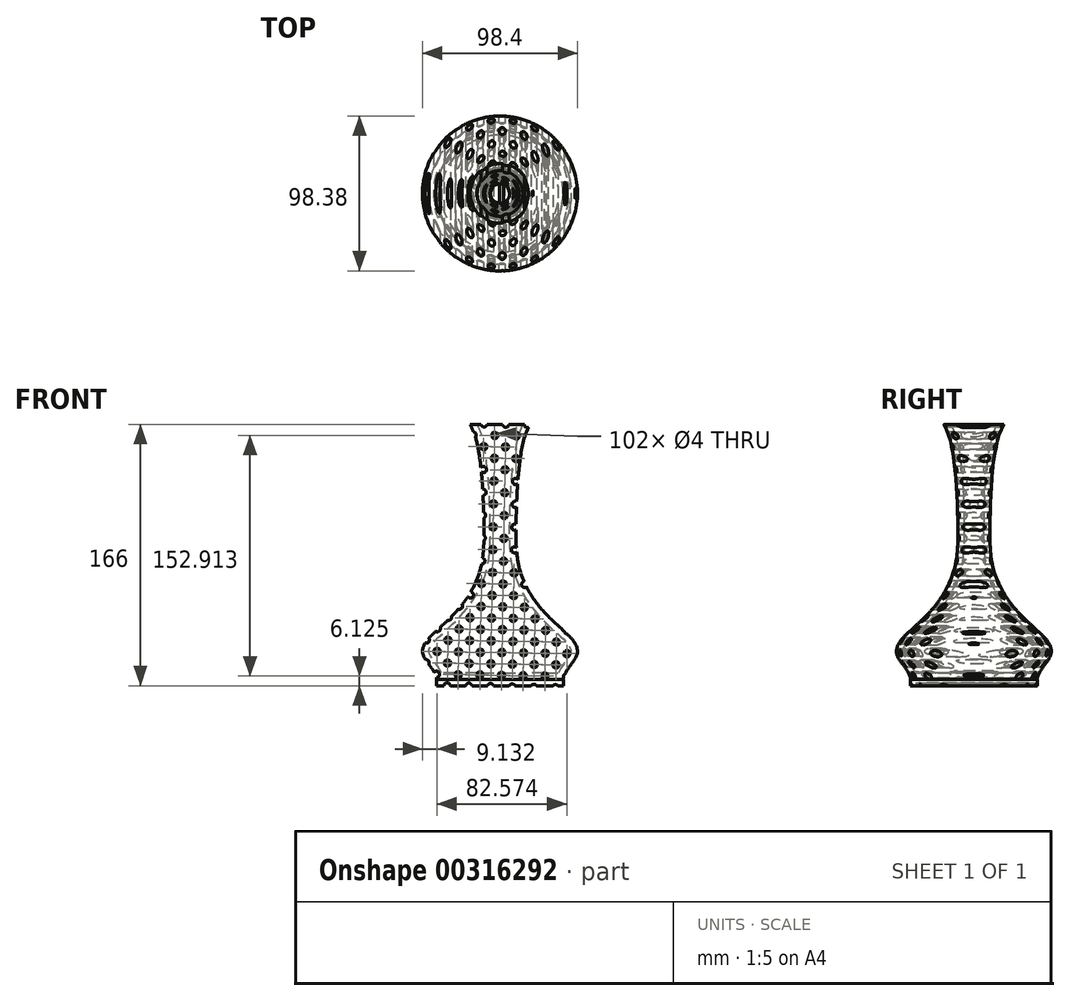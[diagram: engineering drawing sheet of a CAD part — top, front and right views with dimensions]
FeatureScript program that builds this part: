
annotation { "Feature Type Name" : "Feature", "Feature Type Description" : "" }
export const myFeature = defineFeature(function(context is Context, id is Id, definition is map)
    precondition{}
    {
        {
            var Q0;
            Q0=qCreatedBy(makeId("Top.planeOp"),FACE);
            var sketch = newSketch(context, id + "F0", { "sketchPlane" : qUnion([Q0])});
            skCircle(sketch, "E0", {"center": v(0, 0) * mm, "radius": 40 * mm});
            skSolve(sketch);
        }
        {
            var Q0;
            Q0=makeQuery(id+"F0.imprint","IMPRINT",FACE,{"disambiguationData":[TD([[makeQuery(id+"F0.imprint","IMPRINT",EDGE,{"derivedFrom":sQuery(id+"F0.wireOp",EDGE,"E0")}),1.0]])]});
            cPlane(context, id + "F1", {"entities" : qUnion([Q0]), "cplaneType" : CPlaneType.OFFSET, "offset" : 4 * mm, "width" : 150 * mm, "height" : 150 * mm});
        }
        {
            var Q0;
            Q0=qCreatedBy(id+"F1.planeOp",FACE);
            var sketch = newSketch(context, id + "F2", { "sketchPlane" : qUnion([Q0])});
            skCircle(sketch, "E1", {"center": v(0, 0) * mm, "radius": 41.51 * mm});
            skSolve(sketch);
        }
        {
            var Q0;
            Q0=makeQuery(id+"F2.imprint","IMPRINT",FACE,{"disambiguationData":[TD([[makeQuery(id+"F2.imprint","IMPRINT",EDGE,{"derivedFrom":sQuery(id+"F2.wireOp",EDGE,"E1")}),1.0]])]});
            cPlane(context, id + "F3", {"entities" : qUnion([Q0]), "cplaneType" : CPlaneType.OFFSET, "offset" : 6 * mm, "width" : 150 * mm, "height" : 150 * mm});
        }
        {
            var Q0;
            Q0=qCreatedBy(id+"F3.planeOp",FACE);
            var sketch = newSketch(context, id + "F4", { "sketchPlane" : qUnion([Q0])});
            skCircle(sketch, "E2", {"center": v(0, 0) * mm, "radius": 45.5 * mm});
            skSolve(sketch);
        }
        {
            var Q0;
            Q0=makeQuery(id+"F4.imprint","IMPRINT",FACE,{"disambiguationData":[TD([[makeQuery(id+"F4.imprint","IMPRINT",EDGE,{"derivedFrom":sQuery(id+"F4.wireOp",EDGE,"E2")}),1.0]])]});
            cPlane(context, id + "F5", {"entities" : qUnion([Q0]), "cplaneType" : CPlaneType.OFFSET, "offset" : 8 * mm, "width" : 150 * mm, "height" : 150 * mm});
        }
        {
            var Q0;
            Q0=qCreatedBy(id+"F5.planeOp",FACE);
            var sketch = newSketch(context, id + "F6", { "sketchPlane" : qUnion([Q0])});
            skCircle(sketch, "E3", {"center": v(0, 0) * mm, "radius": 49.2 * mm});
            skSolve(sketch);
        }
        {
            var Q0;
            Q0=makeQuery(id+"F6.imprint","IMPRINT",FACE,{"disambiguationData":[TD([[makeQuery(id+"F6.imprint","IMPRINT",EDGE,{"derivedFrom":sQuery(id+"F6.wireOp",EDGE,"E3")}),1.0]])]});
            cPlane(context, id + "F7", {"entities" : qUnion([Q0]), "cplaneType" : CPlaneType.OFFSET, "offset" : 6 * mm, "width" : 150 * mm, "height" : 150 * mm});
        }
        {
            var Q0;
            Q0=qCreatedBy(id+"F7.planeOp",FACE);
            var sketch = newSketch(context, id + "F8", { "sketchPlane" : qUnion([Q0])});
            skCircle(sketch, "E4", {"center": v(0, 0) * mm, "radius": 47 * mm});
            skSolve(sketch);
        }
        {
            var Q0;
            Q0=qCreatedBy(id+"F7.planeOp",FACE);
            cPlane(context, id + "F9", {"entities" : qUnion([Q0]), "cplaneType" : CPlaneType.OFFSET, "offset" : 6 * mm, "width" : 150 * mm, "height" : 150 * mm});
        }
        {
            var Q0;
            Q0=qCreatedBy(id+"F9.planeOp",FACE);
            var sketch = newSketch(context, id + "F10", { "sketchPlane" : qUnion([Q0])});
            skCircle(sketch, "E5", {"center": v(0, 0) * mm, "radius": 41.44 * mm});
            skSolve(sketch);
        }
        {
            var Q0;
            Q0=qCreatedBy(id+"F9.planeOp",FACE);
            cPlane(context, id + "F11", {"entities" : qUnion([Q0]), "cplaneType" : CPlaneType.OFFSET, "offset" : 16 * mm, "width" : 150 * mm, "height" : 150 * mm});
        }
        {
            var Q0;
            Q0=qCreatedBy(id+"F11.planeOp",FACE);
            var sketch = newSketch(context, id + "F12", { "sketchPlane" : qUnion([Q0])});
            skCircle(sketch, "E6", {"center": v(0, 0) * mm, "radius": 25.29 * mm});
            skSolve(sketch);
        }
        {
            var Q0;
            Q0=qCreatedBy(id+"F11.planeOp",FACE);
            cPlane(context, id + "F13", {"entities" : qUnion([Q0]), "cplaneType" : CPlaneType.OFFSET, "offset" : 25 * mm, "width" : 150 * mm, "height" : 150 * mm});
        }
        {
            var Q0;
            Q0=qCreatedBy(id+"F13.planeOp",FACE);
            var sketch = newSketch(context, id + "F14", { "sketchPlane" : qUnion([Q0])});
            skCircle(sketch, "E7", {"center": v(0, 0) * mm, "radius": 12.22 * mm});
            skSolve(sketch);
        }
        {
            var Q0;
            Q0=qCreatedBy(id+"F13.planeOp",FACE);
            cPlane(context, id + "F15", {"entities" : qUnion([Q0]), "cplaneType" : CPlaneType.OFFSET, "offset" : 25 * mm, "width" : 150 * mm, "height" : 150 * mm});
        }
        {
            var Q0;
            Q0=qCreatedBy(id+"F15.planeOp",FACE);
            var sketch = newSketch(context, id + "F16", { "sketchPlane" : qUnion([Q0])});
            skCircle(sketch, "E8", {"center": v(0, 0) * mm, "radius": 10.18 * mm});
            skSolve(sketch);
        }
        {
            var Q0;
            Q0=qCreatedBy(id+"F15.planeOp",FACE);
            cPlane(context, id + "F17", {"entities" : qUnion([Q0]), "cplaneType" : CPlaneType.OFFSET, "offset" : 25 * mm, "width" : 150 * mm, "height" : 150 * mm});
        }
        {
            var Q0;
            Q0=qCreatedBy(id+"F17.planeOp",FACE);
            var sketch = newSketch(context, id + "F18", { "sketchPlane" : qUnion([Q0])});
            skCircle(sketch, "E9", {"center": v(0, 0) * mm, "radius": 11 * mm});
            skSolve(sketch);
        }
        {
            var Q0;
            Q0=qCreatedBy(id+"F17.planeOp",FACE);
            cPlane(context, id + "F19", {"entities" : qUnion([Q0]), "cplaneType" : CPlaneType.OFFSET, "offset" : 25 * mm, "width" : 150 * mm, "height" : 150 * mm});
        }
        {
            var Q0;
            Q0=qCreatedBy(id+"F19.planeOp",FACE);
            var sketch = newSketch(context, id + "F20", { "sketchPlane" : qUnion([Q0])});
            skCircle(sketch, "E10", {"center": v(0, 0) * mm, "radius": 13.75 * mm});
            skSolve(sketch);
        }
        {
            var Q0;
            Q0=qCreatedBy(id+"F19.planeOp",FACE);
            cPlane(context, id + "F21", {"entities" : qUnion([Q0]), "cplaneType" : CPlaneType.OFFSET, "offset" : 10 * mm, "width" : 150 * mm, "height" : 150 * mm});
        }
        {
            var Q0;
            Q0=qCreatedBy(id+"F21.planeOp",FACE);
            var sketch = newSketch(context, id + "F22", { "sketchPlane" : qUnion([Q0])});
            skCircle(sketch, "E11", {"center": v(0, 0) * mm, "radius": 16.33 * mm});
            skSolve(sketch);
        }
        {
            var Q0;
            Q0=qCreatedBy(id+"F21.planeOp",FACE);
            cPlane(context, id + "F23", {"entities" : qUnion([Q0]), "cplaneType" : CPlaneType.OFFSET, "offset" : 6 * mm, "width" : 150 * mm, "height" : 150 * mm});
        }
        {
            var Q0;
            Q0=qCreatedBy(id+"F23.planeOp",FACE);
            var sketch = newSketch(context, id + "F24", { "sketchPlane" : qUnion([Q0])});
            skCircle(sketch, "E12", {"center": v(0, 0) * mm, "radius": 18.94 * mm});
            skSolve(sketch);
        }
        {
            var Q0;
            Q0=qSketchRegion(id+"F0",true);
            var Q1;
            Q1=qSketchRegion(id+"F2",true);
            var Q2;
            Q2=qSketchRegion(id+"F4",true);
            var Q3;
            Q3=qSketchRegion(id+"F6",true);
            var Q4;
            Q4=qSketchRegion(id+"F8",true);
            var Q5;
            Q5=qSketchRegion(id+"F10",true);
            var Q6;
            Q6=qSketchRegion(id+"F12",true);
            var Q7;
            Q7=qSketchRegion(id+"F14",true);
            var Q8;
            Q8=qSketchRegion(id+"F16",true);
            var Q9;
            Q9=qSketchRegion(id+"F18",true);
            var Q10;
            Q10=qSketchRegion(id+"F20",true);
            var Q11;
            Q11=qSketchRegion(id+"F22",true);
            var Q12;
            Q12=qSketchRegion(id+"F24",true);
            loft(context, id + "F25", {"sheetProfilesArray" : [{ "sheetProfileEntities" : qUnion([Q0]) }, { "sheetProfileEntities" : qUnion([Q1]) }, { "sheetProfileEntities" : qUnion([Q2]) }, { "sheetProfileEntities" : qUnion([Q3]) }, { "sheetProfileEntities" : qUnion([Q4]) }, { "sheetProfileEntities" : qUnion([Q5]) }, { "sheetProfileEntities" : qUnion([Q6]) }, { "sheetProfileEntities" : qUnion([Q7]) }, { "sheetProfileEntities" : qUnion([Q8]) }, { "sheetProfileEntities" : qUnion([Q9]) }, { "sheetProfileEntities" : qUnion([Q10]) }, { "sheetProfileEntities" : qUnion([Q11]) }, { "sheetProfileEntities" : qUnion([Q12]) }]});
        }
        {
            var Q0;
            Q0=makeQuery(id+"F25.opLoft","CAP_FACE",FACE,{"disambiguationData":[OSD([makeQuery(id+"F24.imprint","IMPRINT",FACE,{"disambiguationData":[TD([[makeQuery(id+"F24.imprint","IMPRINT",EDGE,{"derivedFrom":sQuery(id+"F24.wireOp",EDGE,"E12")}),1.0]])]})])],"isStart":true});
            shell(context, id + "F26", {"entities" : qUnion([Q0]), "thickness" : 4 * mm});
        }
        {
            var Q0;
            Q0=qCreatedBy(makeId("Top.planeOp"),FACE);
            var sketch = newSketch(context, id + "F27", { "sketchPlane" : qUnion([Q0])});
            skCircle(sketch, "E13", {"center": v(0, 0) * mm, "radius": 40.24 * mm});
            skSolve(sketch);
        }
        {
            var Q0;
            Q0=qSketchRegion(id+"F27",true);
            extrude(context, id + "F28", {"entities" : qUnion([Q0]), "operationType" : NewBodyOperationType.ADD, "oppositeDirection" : true, "depth" : 4 * mm});
        }
        {
            var Q0;
            Q0=qCreatedBy(makeId("Front.planeOp"),FACE);
            var sketch = newSketch(context, id + "F29", { "sketchPlane" : qUnion([Q0])});
            skCircle(sketch, "E14", {"center": v(0, -55.44) * mm, "radius": 2 * mm});
            skCircle(sketch, "E15.0.1.0", {"center": v(-6.76, -48.08) * mm, "radius": 2 * mm});
            skCircle(sketch, "E15.0.2.0", {"center": v(-13.52, -40.7) * mm, "radius": 2 * mm});
            skCircle(sketch, "E15.0.3.0", {"center": v(-20.28, -33.34) * mm, "radius": 2 * mm});
            skCircle(sketch, "E15.0.4.0", {"center": v(-27.04, -25.97) * mm, "radius": 2 * mm});
            skCircle(sketch, "E15.0.5.0", {"center": v(-33.8, -18.6) * mm, "radius": 2 * mm});
            skCircle(sketch, "E15.0.6.0", {"center": v(-40.56, -11.23) * mm, "radius": 2 * mm});
            skCircle(sketch, "E15.0.7.0", {"center": v(-47.32, -3.86) * mm, "radius": 2 * mm});
            skCircle(sketch, "E15.0.8.0", {"center": v(-54.07, 3.51) * mm, "radius": 2 * mm});
            skCircle(sketch, "E15.0.9.0", {"center": v(-60.83, 10.88) * mm, "radius": 2 * mm});
            skCircle(sketch, "E15.0.10.0", {"center": v(-67.6, 18.25) * mm, "radius": 2 * mm});
            skCircle(sketch, "E15.0.11.0", {"center": v(-74.35, 25.62) * mm, "radius": 2 * mm});
            skCircle(sketch, "E15.0.12.0", {"center": v(-81.11, 33) * mm, "radius": 2 * mm});
            skCircle(sketch, "E15.0.13.0", {"center": v(-87.87, 40.36) * mm, "radius": 2 * mm});
            skCircle(sketch, "E15.0.14.0", {"center": v(-94.63, 47.73) * mm, "radius": 2 * mm});
            skCircle(sketch, "E15.0.15.0", {"center": v(-101.39, 55.1) * mm, "radius": 2 * mm});
            skCircle(sketch, "E15.0.16.0", {"center": v(-108.15, 62.47) * mm, "radius": 2 * mm});
            skCircle(sketch, "E15.0.17.0", {"center": v(-114.9, 69.84) * mm, "radius": 2 * mm});
            skCircle(sketch, "E15.0.18.0", {"center": v(-121.67, 77.2) * mm, "radius": 2 * mm});
            skCircle(sketch, "E15.0.19.0", {"center": v(-128.43, 84.58) * mm, "radius": 2 * mm});
            skCircle(sketch, "E15.0.20.0", {"center": v(-135.19, 91.95) * mm, "radius": 2 * mm});
            skCircle(sketch, "E15.0.21.0", {"center": v(-141.95, 99.32) * mm, "radius": 2 * mm});
            skCircle(sketch, "E15.0.22.0", {"center": v(-148.7, 106.69) * mm, "radius": 2 * mm});
            skCircle(sketch, "E15.0.23.0", {"center": v(-155.46, 114.06) * mm, "radius": 2 * mm});
            skCircle(sketch, "E15.0.24.0", {"center": v(-162.22, 121.43) * mm, "radius": 2 * mm});
            skCircle(sketch, "E15.1.0.0", {"center": v(7, -48.3) * mm, "radius": 2 * mm});
            skCircle(sketch, "E15.1.1.0", {"center": v(0.24, -40.94) * mm, "radius": 2 * mm});
            skCircle(sketch, "E15.1.2.0", {"center": v(-6.52, -33.57) * mm, "radius": 2 * mm});
            skCircle(sketch, "E15.1.3.0", {"center": v(-13.27, -26.2) * mm, "radius": 2 * mm});
            skCircle(sketch, "E15.1.4.0", {"center": v(-20.03, -18.83) * mm, "radius": 2 * mm});
            skCircle(sketch, "E15.1.5.0", {"center": v(-26.8, -11.46) * mm, "radius": 2 * mm});
            skCircle(sketch, "E15.1.6.0", {"center": v(-33.55, -4.09) * mm, "radius": 2 * mm});
            skCircle(sketch, "E15.1.7.0", {"center": v(-40.31, 3.28) * mm, "radius": 2 * mm});
            skCircle(sketch, "E15.1.8.0", {"center": v(-47.07, 10.65) * mm, "radius": 2 * mm});
            skCircle(sketch, "E15.1.9.0", {"center": v(-53.83, 18.02) * mm, "radius": 2 * mm});
            skCircle(sketch, "E15.1.10.0", {"center": v(-60.6, 25.4) * mm, "radius": 2 * mm});
            skCircle(sketch, "E15.1.11.0", {"center": v(-67.35, 32.76) * mm, "radius": 2 * mm});
            skCircle(sketch, "E15.1.12.0", {"center": v(-74.1, 40.13) * mm, "radius": 2 * mm});
            skCircle(sketch, "E15.1.13.0", {"center": v(-80.87, 47.5) * mm, "radius": 2 * mm});
            skCircle(sketch, "E15.1.14.0", {"center": v(-87.63, 54.87) * mm, "radius": 2 * mm});
            skCircle(sketch, "E15.1.15.0", {"center": v(-94.39, 62.24) * mm, "radius": 2 * mm});
            skCircle(sketch, "E15.1.16.0", {"center": v(-101.15, 69.6) * mm, "radius": 2 * mm});
            skCircle(sketch, "E15.1.17.0", {"center": v(-107.9, 76.98) * mm, "radius": 2 * mm});
            skCircle(sketch, "E15.1.18.0", {"center": v(-114.66, 84.35) * mm, "radius": 2 * mm});
            skCircle(sketch, "E15.1.19.0", {"center": v(-121.42, 91.72) * mm, "radius": 2 * mm});
            skCircle(sketch, "E15.1.20.0", {"center": v(-128.18, 99.09) * mm, "radius": 2 * mm});
            skCircle(sketch, "E15.1.21.0", {"center": v(-134.94, 106.46) * mm, "radius": 2 * mm});
            skCircle(sketch, "E15.1.22.0", {"center": v(-141.7, 113.83) * mm, "radius": 2 * mm});
            skCircle(sketch, "E15.1.23.0", {"center": v(-148.46, 121.2) * mm, "radius": 2 * mm});
            skCircle(sketch, "E15.1.24.0", {"center": v(-155.22, 128.57) * mm, "radius": 2 * mm});
            skCircle(sketch, "E15.2.0.0", {"center": v(14, -41.17) * mm, "radius": 2 * mm});
            skCircle(sketch, "E15.2.1.0", {"center": v(7.25, -33.8) * mm, "radius": 2 * mm});
            skCircle(sketch, "E15.2.2.0", {"center": v(0.49, -26.43) * mm, "radius": 2 * mm});
            skCircle(sketch, "E15.2.3.0", {"center": v(-6.27, -19.06) * mm, "radius": 2 * mm});
            skCircle(sketch, "E15.2.4.0", {"center": v(-13.03, -11.69) * mm, "radius": 2 * mm});
            skCircle(sketch, "E15.2.5.0", {"center": v(-19.8, -4.32) * mm, "radius": 2 * mm});
            skCircle(sketch, "E15.2.6.0", {"center": v(-26.55, 3.05) * mm, "radius": 2 * mm});
            skCircle(sketch, "E15.2.7.0", {"center": v(-33.3, 10.42) * mm, "radius": 2 * mm});
            skCircle(sketch, "E15.2.8.0", {"center": v(-40.07, 17.79) * mm, "radius": 2 * mm});
            skCircle(sketch, "E15.2.9.0", {"center": v(-46.83, 25.16) * mm, "radius": 2 * mm});
            skCircle(sketch, "E15.2.10.0", {"center": v(-53.59, 32.53) * mm, "radius": 2 * mm});
            skCircle(sketch, "E15.2.11.0", {"center": v(-60.35, 39.9) * mm, "radius": 2 * mm});
            skCircle(sketch, "E15.2.12.0", {"center": v(-67.1, 47.27) * mm, "radius": 2 * mm});
            skCircle(sketch, "E15.2.13.0", {"center": v(-73.86, 54.64) * mm, "radius": 2 * mm});
            skCircle(sketch, "E15.2.14.0", {"center": v(-80.62, 62) * mm, "radius": 2 * mm});
            skCircle(sketch, "E15.2.15.0", {"center": v(-87.38, 69.38) * mm, "radius": 2 * mm});
            skCircle(sketch, "E15.2.16.0", {"center": v(-94.14, 76.75) * mm, "radius": 2 * mm});
            skCircle(sketch, "E15.2.17.0", {"center": v(-100.9, 84.12) * mm, "radius": 2 * mm});
            skCircle(sketch, "E15.2.18.0", {"center": v(-107.66, 91.49) * mm, "radius": 2 * mm});
            skCircle(sketch, "E15.2.19.0", {"center": v(-114.42, 98.86) * mm, "radius": 2 * mm});
            skCircle(sketch, "E15.2.20.0", {"center": v(-121.18, 106.23) * mm, "radius": 2 * mm});
            skCircle(sketch, "E15.2.21.0", {"center": v(-127.94, 113.6) * mm, "radius": 2 * mm});
            skCircle(sketch, "E15.2.22.0", {"center": v(-134.7, 120.96) * mm, "radius": 2 * mm});
            skCircle(sketch, "E15.2.23.0", {"center": v(-141.46, 128.33) * mm, "radius": 2 * mm});
            skCircle(sketch, "E15.2.24.0", {"center": v(-148.22, 135.7) * mm, "radius": 2 * mm});
            skCircle(sketch, "E15.3.0.0", {"center": v(21, -34.03) * mm, "radius": 2 * mm});
            skCircle(sketch, "E15.3.1.0", {"center": v(14.25, -26.66) * mm, "radius": 2 * mm});
            skCircle(sketch, "E15.3.2.0", {"center": v(7.5, -19.3) * mm, "radius": 2 * mm});
            skCircle(sketch, "E15.3.3.0", {"center": v(0.73, -11.92) * mm, "radius": 2 * mm});
            skCircle(sketch, "E15.3.4.0", {"center": v(-6.03, -4.55) * mm, "radius": 2 * mm});
            skCircle(sketch, "E15.3.5.0", {"center": v(-12.79, 2.82) * mm, "radius": 2 * mm});
            skCircle(sketch, "E15.3.6.0", {"center": v(-19.55, 10.19) * mm, "radius": 2 * mm});
            skCircle(sketch, "E15.3.7.0", {"center": v(-26.3, 17.56) * mm, "radius": 2 * mm});
            skCircle(sketch, "E15.3.8.0", {"center": v(-33.07, 24.93) * mm, "radius": 2 * mm});
            skCircle(sketch, "E15.3.9.0", {"center": v(-39.82, 32.3) * mm, "radius": 2 * mm});
            skCircle(sketch, "E15.3.10.0", {"center": v(-46.58, 39.67) * mm, "radius": 2 * mm});
            skCircle(sketch, "E15.3.11.0", {"center": v(-53.34, 47.04) * mm, "radius": 2 * mm});
            skCircle(sketch, "E15.3.12.0", {"center": v(-60.1, 54.4) * mm, "radius": 2 * mm});
            skCircle(sketch, "E15.3.13.0", {"center": v(-66.86, 61.78) * mm, "radius": 2 * mm});
            skCircle(sketch, "E15.3.14.0", {"center": v(-73.62, 69.15) * mm, "radius": 2 * mm});
            skCircle(sketch, "E15.3.15.0", {"center": v(-80.38, 76.52) * mm, "radius": 2 * mm});
            skCircle(sketch, "E15.3.16.0", {"center": v(-87.14, 83.89) * mm, "radius": 2 * mm});
            skCircle(sketch, "E15.3.17.0", {"center": v(-93.9, 91.25) * mm, "radius": 2 * mm});
            skCircle(sketch, "E15.3.18.0", {"center": v(-100.66, 98.62) * mm, "radius": 2 * mm});
            skCircle(sketch, "E15.3.19.0", {"center": v(-107.42, 106) * mm, "radius": 2 * mm});
            skCircle(sketch, "E15.3.20.0", {"center": v(-114.18, 113.36) * mm, "radius": 2 * mm});
            skCircle(sketch, "E15.3.21.0", {"center": v(-120.94, 120.73) * mm, "radius": 2 * mm});
            skCircle(sketch, "E15.3.22.0", {"center": v(-127.7, 128.1) * mm, "radius": 2 * mm});
            skCircle(sketch, "E15.3.23.0", {"center": v(-134.45, 135.47) * mm, "radius": 2 * mm});
            skCircle(sketch, "E15.3.24.0", {"center": v(-141.21, 142.84) * mm, "radius": 2 * mm});
            skCircle(sketch, "E15.4.0.0", {"center": v(28.01, -26.9) * mm, "radius": 2 * mm});
            skCircle(sketch, "E15.4.1.0", {"center": v(21.25, -19.52) * mm, "radius": 2 * mm});
            skCircle(sketch, "E15.4.2.0", {"center": v(14.5, -12.15) * mm, "radius": 2 * mm});
            skCircle(sketch, "E15.4.3.0", {"center": v(7.73, -4.78) * mm, "radius": 2 * mm});
            skCircle(sketch, "E15.4.4.0", {"center": v(0.97, 2.59) * mm, "radius": 2 * mm});
            skCircle(sketch, "E15.4.5.0", {"center": v(-5.78, 9.96) * mm, "radius": 2 * mm});
            skCircle(sketch, "E15.4.6.0", {"center": v(-12.54, 17.33) * mm, "radius": 2 * mm});
            skCircle(sketch, "E15.4.7.0", {"center": v(-19.3, 24.7) * mm, "radius": 2 * mm});
            skCircle(sketch, "E15.4.8.0", {"center": v(-26.06, 32.07) * mm, "radius": 2 * mm});
            skCircle(sketch, "E15.4.9.0", {"center": v(-32.82, 39.44) * mm, "radius": 2 * mm});
            skCircle(sketch, "E15.4.10.0", {"center": v(-39.58, 46.8) * mm, "radius": 2 * mm});
            skCircle(sketch, "E15.4.11.0", {"center": v(-46.34, 54.18) * mm, "radius": 2 * mm});
            skCircle(sketch, "E15.4.12.0", {"center": v(-53.1, 61.54) * mm, "radius": 2 * mm});
            skCircle(sketch, "E15.4.13.0", {"center": v(-59.86, 68.91) * mm, "radius": 2 * mm});
            skCircle(sketch, "E15.4.14.0", {"center": v(-66.62, 76.28) * mm, "radius": 2 * mm});
            skCircle(sketch, "E15.4.15.0", {"center": v(-73.38, 83.65) * mm, "radius": 2 * mm});
            skCircle(sketch, "E15.4.16.0", {"center": v(-80.14, 91.02) * mm, "radius": 2 * mm});
            skCircle(sketch, "E15.4.17.0", {"center": v(-86.9, 98.4) * mm, "radius": 2 * mm});
            skCircle(sketch, "E15.4.18.0", {"center": v(-93.66, 105.76) * mm, "radius": 2 * mm});
            skCircle(sketch, "E15.4.19.0", {"center": v(-100.41, 113.13) * mm, "radius": 2 * mm});
            skCircle(sketch, "E15.4.20.0", {"center": v(-107.17, 120.5) * mm, "radius": 2 * mm});
            skCircle(sketch, "E15.4.21.0", {"center": v(-113.93, 127.87) * mm, "radius": 2 * mm});
            skCircle(sketch, "E15.4.22.0", {"center": v(-120.7, 135.24) * mm, "radius": 2 * mm});
            skCircle(sketch, "E15.4.23.0", {"center": v(-127.45, 142.61) * mm, "radius": 2 * mm});
            skCircle(sketch, "E15.4.24.0", {"center": v(-134.21, 149.98) * mm, "radius": 2 * mm});
            skCircle(sketch, "E15.5.0.0", {"center": v(35.02, -19.75) * mm, "radius": 2 * mm});
            skCircle(sketch, "E15.5.1.0", {"center": v(28.26, -12.38) * mm, "radius": 2 * mm});
            skCircle(sketch, "E15.5.2.0", {"center": v(21.5, -5.01) * mm, "radius": 2 * mm});
            skCircle(sketch, "E15.5.3.0", {"center": v(14.74, 2.36) * mm, "radius": 2 * mm});
            skCircle(sketch, "E15.5.4.0", {"center": v(7.98, 9.73) * mm, "radius": 2 * mm});
            skCircle(sketch, "E15.5.5.0", {"center": v(1.22, 17.1) * mm, "radius": 2 * mm});
            skCircle(sketch, "E15.5.6.0", {"center": v(-5.54, 24.47) * mm, "radius": 2 * mm});
            skCircle(sketch, "E15.5.7.0", {"center": v(-12.3, 31.84) * mm, "radius": 2 * mm});
            skCircle(sketch, "E15.5.8.0", {"center": v(-19.06, 39.2) * mm, "radius": 2 * mm});
            skCircle(sketch, "E15.5.9.0", {"center": v(-25.82, 46.57) * mm, "radius": 2 * mm});
            skCircle(sketch, "E15.5.10.0", {"center": v(-32.58, 53.94) * mm, "radius": 2 * mm});
            skCircle(sketch, "E15.5.11.0", {"center": v(-39.34, 61.31) * mm, "radius": 2 * mm});
            skCircle(sketch, "E15.5.12.0", {"center": v(-46.1, 68.68) * mm, "radius": 2 * mm});
            skCircle(sketch, "E15.5.13.0", {"center": v(-52.86, 76.05) * mm, "radius": 2 * mm});
            skCircle(sketch, "E15.5.14.0", {"center": v(-59.62, 83.42) * mm, "radius": 2 * mm});
            skCircle(sketch, "E15.5.15.0", {"center": v(-66.37, 90.8) * mm, "radius": 2 * mm});
            skCircle(sketch, "E15.5.16.0", {"center": v(-73.13, 98.16) * mm, "radius": 2 * mm});
            skCircle(sketch, "E15.5.17.0", {"center": v(-79.9, 105.53) * mm, "radius": 2 * mm});
            skCircle(sketch, "E15.5.18.0", {"center": v(-86.65, 112.9) * mm, "radius": 2 * mm});
            skCircle(sketch, "E15.5.19.0", {"center": v(-93.41, 120.27) * mm, "radius": 2 * mm});
            skCircle(sketch, "E15.5.20.0", {"center": v(-100.17, 127.64) * mm, "radius": 2 * mm});
            skCircle(sketch, "E15.5.21.0", {"center": v(-106.93, 135.01) * mm, "radius": 2 * mm});
            skCircle(sketch, "E15.5.22.0", {"center": v(-113.69, 142.38) * mm, "radius": 2 * mm});
            skCircle(sketch, "E15.5.23.0", {"center": v(-120.45, 149.75) * mm, "radius": 2 * mm});
            skCircle(sketch, "E15.5.24.0", {"center": v(-127.2, 157.12) * mm, "radius": 2 * mm});
            skCircle(sketch, "E15.6.0.0", {"center": v(42.02, -12.61) * mm, "radius": 2 * mm});
            skCircle(sketch, "E15.6.1.0", {"center": v(35.26, -5.24) * mm, "radius": 2 * mm});
            skCircle(sketch, "E15.6.2.0", {"center": v(28.5, 2.13) * mm, "radius": 2 * mm});
            skCircle(sketch, "E15.6.3.0", {"center": v(21.74, 9.5) * mm, "radius": 2 * mm});
            skCircle(sketch, "E15.6.4.0", {"center": v(14.98, 16.86) * mm, "radius": 2 * mm});
            skCircle(sketch, "E15.6.5.0", {"center": v(8.22, 24.23) * mm, "radius": 2 * mm});
            skCircle(sketch, "E15.6.6.0", {"center": v(1.46, 31.6) * mm, "radius": 2 * mm});
            skCircle(sketch, "E15.6.7.0", {"center": v(-5.3, 38.97) * mm, "radius": 2 * mm});
            skCircle(sketch, "E15.6.8.0", {"center": v(-12.06, 46.34) * mm, "radius": 2 * mm});
            skCircle(sketch, "E15.6.9.0", {"center": v(-18.82, 53.71) * mm, "radius": 2 * mm});
            skCircle(sketch, "E15.6.10.0", {"center": v(-25.57, 61.08) * mm, "radius": 2 * mm});
            skCircle(sketch, "E15.6.11.0", {"center": v(-32.33, 68.45) * mm, "radius": 2 * mm});
            skCircle(sketch, "E15.6.12.0", {"center": v(-39.1, 75.82) * mm, "radius": 2 * mm});
            skCircle(sketch, "E15.6.13.0", {"center": v(-45.85, 83.2) * mm, "radius": 2 * mm});
            skCircle(sketch, "E15.6.14.0", {"center": v(-52.61, 90.56) * mm, "radius": 2 * mm});
            skCircle(sketch, "E15.6.15.0", {"center": v(-59.37, 97.93) * mm, "radius": 2 * mm});
            skCircle(sketch, "E15.6.16.0", {"center": v(-66.13, 105.3) * mm, "radius": 2 * mm});
            skCircle(sketch, "E15.6.17.0", {"center": v(-72.9, 112.67) * mm, "radius": 2 * mm});
            skCircle(sketch, "E15.6.18.0", {"center": v(-79.65, 120.04) * mm, "radius": 2 * mm});
            skCircle(sketch, "E15.6.19.0", {"center": v(-86.4, 127.4) * mm, "radius": 2 * mm});
            skCircle(sketch, "E15.6.20.0", {"center": v(-93.17, 134.78) * mm, "radius": 2 * mm});
            skCircle(sketch, "E15.6.21.0", {"center": v(-99.93, 142.15) * mm, "radius": 2 * mm});
            skCircle(sketch, "E15.6.22.0", {"center": v(-106.69, 149.52) * mm, "radius": 2 * mm});
            skCircle(sketch, "E15.6.23.0", {"center": v(-113.45, 156.89) * mm, "radius": 2 * mm});
            skCircle(sketch, "E15.6.24.0", {"center": v(-120.2, 164.26) * mm, "radius": 2 * mm});
            skCircle(sketch, "E15.7.0.0", {"center": v(49.02, -5.48) * mm, "radius": 2 * mm});
            skCircle(sketch, "E15.7.1.0", {"center": v(42.26, 1.9) * mm, "radius": 2 * mm});
            skCircle(sketch, "E15.7.2.0", {"center": v(35.5, 9.26) * mm, "radius": 2 * mm});
            skCircle(sketch, "E15.7.3.0", {"center": v(28.74, 16.63) * mm, "radius": 2 * mm});
            skCircle(sketch, "E15.7.4.0", {"center": v(21.98, 24) * mm, "radius": 2 * mm});
            skCircle(sketch, "E15.7.5.0", {"center": v(15.22, 31.37) * mm, "radius": 2 * mm});
            skCircle(sketch, "E15.7.6.0", {"center": v(8.47, 38.74) * mm, "radius": 2 * mm});
            skCircle(sketch, "E15.7.7.0", {"center": v(1.7, 46.11) * mm, "radius": 2 * mm});
            skCircle(sketch, "E15.7.8.0", {"center": v(-5.05, 53.48) * mm, "radius": 2 * mm});
            skCircle(sketch, "E15.7.9.0", {"center": v(-11.81, 60.85) * mm, "radius": 2 * mm});
            skCircle(sketch, "E15.7.10.0", {"center": v(-18.57, 68.22) * mm, "radius": 2 * mm});
            skCircle(sketch, "E15.7.11.0", {"center": v(-25.33, 75.6) * mm, "radius": 2 * mm});
            skCircle(sketch, "E15.7.12.0", {"center": v(-32.1, 82.96) * mm, "radius": 2 * mm});
            skCircle(sketch, "E15.7.13.0", {"center": v(-38.85, 90.33) * mm, "radius": 2 * mm});
            skCircle(sketch, "E15.7.14.0", {"center": v(-45.6, 97.7) * mm, "radius": 2 * mm});
            skCircle(sketch, "E15.7.15.0", {"center": v(-52.37, 105.07) * mm, "radius": 2 * mm});
            skCircle(sketch, "E15.7.16.0", {"center": v(-59.13, 112.44) * mm, "radius": 2 * mm});
            skCircle(sketch, "E15.7.17.0", {"center": v(-65.89, 119.8) * mm, "radius": 2 * mm});
            skCircle(sketch, "E15.7.18.0", {"center": v(-72.65, 127.18) * mm, "radius": 2 * mm});
            skCircle(sketch, "E15.7.19.0", {"center": v(-79.4, 134.55) * mm, "radius": 2 * mm});
            skCircle(sketch, "E15.7.20.0", {"center": v(-86.16, 141.92) * mm, "radius": 2 * mm});
            skCircle(sketch, "E15.7.21.0", {"center": v(-92.92, 149.29) * mm, "radius": 2 * mm});
            skCircle(sketch, "E15.7.22.0", {"center": v(-99.68, 156.66) * mm, "radius": 2 * mm});
            skCircle(sketch, "E15.7.23.0", {"center": v(-106.44, 164.03) * mm, "radius": 2 * mm});
            skCircle(sketch, "E15.7.24.0", {"center": v(-113.2, 171.4) * mm, "radius": 2 * mm});
            skCircle(sketch, "E15.8.0.0", {"center": v(56.02, 1.66) * mm, "radius": 2 * mm});
            skCircle(sketch, "E15.8.1.0", {"center": v(49.26, 9.03) * mm, "radius": 2 * mm});
            skCircle(sketch, "E15.8.2.0", {"center": v(42.5, 16.4) * mm, "radius": 2 * mm});
            skCircle(sketch, "E15.8.3.0", {"center": v(35.75, 23.77) * mm, "radius": 2 * mm});
            skCircle(sketch, "E15.8.4.0", {"center": v(28.99, 31.14) * mm, "radius": 2 * mm});
            skCircle(sketch, "E15.8.5.0", {"center": v(22.23, 38.51) * mm, "radius": 2 * mm});
            skCircle(sketch, "E15.8.6.0", {"center": v(15.47, 45.88) * mm, "radius": 2 * mm});
            skCircle(sketch, "E15.8.7.0", {"center": v(8.7, 53.25) * mm, "radius": 2 * mm});
            skCircle(sketch, "E15.8.8.0", {"center": v(1.95, 60.62) * mm, "radius": 2 * mm});
            skCircle(sketch, "E15.8.9.0", {"center": v(-4.8, 67.99) * mm, "radius": 2 * mm});
            skCircle(sketch, "E15.8.10.0", {"center": v(-11.57, 75.36) * mm, "radius": 2 * mm});
            skCircle(sketch, "E15.8.11.0", {"center": v(-18.33, 82.73) * mm, "radius": 2 * mm});
            skCircle(sketch, "E15.8.12.0", {"center": v(-25.09, 90.1) * mm, "radius": 2 * mm});
            skCircle(sketch, "E15.8.13.0", {"center": v(-31.85, 97.47) * mm, "radius": 2 * mm});
            skCircle(sketch, "E15.8.14.0", {"center": v(-38.6, 104.84) * mm, "radius": 2 * mm});
            skCircle(sketch, "E15.8.15.0", {"center": v(-45.37, 112.2) * mm, "radius": 2 * mm});
            skCircle(sketch, "E15.8.16.0", {"center": v(-52.12, 119.58) * mm, "radius": 2 * mm});
            skCircle(sketch, "E15.8.17.0", {"center": v(-58.88, 126.95) * mm, "radius": 2 * mm});
            skCircle(sketch, "E15.8.18.0", {"center": v(-65.64, 134.32) * mm, "radius": 2 * mm});
            skCircle(sketch, "E15.8.19.0", {"center": v(-72.4, 141.69) * mm, "radius": 2 * mm});
            skCircle(sketch, "E15.8.20.0", {"center": v(-79.16, 149.06) * mm, "radius": 2 * mm});
            skCircle(sketch, "E15.8.21.0", {"center": v(-85.92, 156.43) * mm, "radius": 2 * mm});
            skCircle(sketch, "E15.8.22.0", {"center": v(-92.68, 163.8) * mm, "radius": 2 * mm});
            skCircle(sketch, "E15.8.23.0", {"center": v(-99.44, 171.16) * mm, "radius": 2 * mm});
            skCircle(sketch, "E15.8.24.0", {"center": v(-106.2, 178.53) * mm, "radius": 2 * mm});
            skCircle(sketch, "E15.9.0.0", {"center": v(63.03, 8.8) * mm, "radius": 2 * mm});
            skCircle(sketch, "E15.9.1.0", {"center": v(56.27, 16.17) * mm, "radius": 2 * mm});
            skCircle(sketch, "E15.9.2.0", {"center": v(49.5, 23.54) * mm, "radius": 2 * mm});
            skCircle(sketch, "E15.9.3.0", {"center": v(42.75, 30.91) * mm, "radius": 2 * mm});
            skCircle(sketch, "E15.9.4.0", {"center": v(36, 38.28) * mm, "radius": 2 * mm});
            skCircle(sketch, "E15.9.5.0", {"center": v(29.23, 45.65) * mm, "radius": 2 * mm});
            skCircle(sketch, "E15.9.6.0", {"center": v(22.47, 53.02) * mm, "radius": 2 * mm});
            skCircle(sketch, "E15.9.7.0", {"center": v(15.71, 60.39) * mm, "radius": 2 * mm});
            skCircle(sketch, "E15.9.8.0", {"center": v(8.95, 67.76) * mm, "radius": 2 * mm});
            skCircle(sketch, "E15.9.9.0", {"center": v(2.2, 75.13) * mm, "radius": 2 * mm});
            skCircle(sketch, "E15.9.10.0", {"center": v(-4.57, 82.5) * mm, "radius": 2 * mm});
            skCircle(sketch, "E15.9.11.0", {"center": v(-11.33, 89.87) * mm, "radius": 2 * mm});
            skCircle(sketch, "E15.9.12.0", {"center": v(-18.08, 97.24) * mm, "radius": 2 * mm});
            skCircle(sketch, "E15.9.13.0", {"center": v(-24.84, 104.6) * mm, "radius": 2 * mm});
            skCircle(sketch, "E15.9.14.0", {"center": v(-31.6, 111.98) * mm, "radius": 2 * mm});
            skCircle(sketch, "E15.9.15.0", {"center": v(-38.36, 119.35) * mm, "radius": 2 * mm});
            skCircle(sketch, "E15.9.16.0", {"center": v(-45.12, 126.72) * mm, "radius": 2 * mm});
            skCircle(sketch, "E15.9.17.0", {"center": v(-51.88, 134.09) * mm, "radius": 2 * mm});
            skCircle(sketch, "E15.9.18.0", {"center": v(-58.64, 141.46) * mm, "radius": 2 * mm});
            skCircle(sketch, "E15.9.19.0", {"center": v(-65.4, 148.82) * mm, "radius": 2 * mm});
            skCircle(sketch, "E15.9.20.0", {"center": v(-72.16, 156.2) * mm, "radius": 2 * mm});
            skCircle(sketch, "E15.9.21.0", {"center": v(-78.92, 163.56) * mm, "radius": 2 * mm});
            skCircle(sketch, "E15.9.22.0", {"center": v(-85.68, 170.93) * mm, "radius": 2 * mm});
            skCircle(sketch, "E15.9.23.0", {"center": v(-92.44, 178.3) * mm, "radius": 2 * mm});
            skCircle(sketch, "E15.9.24.0", {"center": v(-99.2, 185.67) * mm, "radius": 2 * mm});
            skCircle(sketch, "E15.10.0.0", {"center": v(70.03, 15.94) * mm, "radius": 2 * mm});
            skCircle(sketch, "E15.10.1.0", {"center": v(63.27, 23.3) * mm, "radius": 2 * mm});
            skCircle(sketch, "E15.10.2.0", {"center": v(56.51, 30.68) * mm, "radius": 2 * mm});
            skCircle(sketch, "E15.10.3.0", {"center": v(49.75, 38.05) * mm, "radius": 2 * mm});
            skCircle(sketch, "E15.10.4.0", {"center": v(43, 45.42) * mm, "radius": 2 * mm});
            skCircle(sketch, "E15.10.5.0", {"center": v(36.23, 52.79) * mm, "radius": 2 * mm});
            skCircle(sketch, "E15.10.6.0", {"center": v(29.47, 60.16) * mm, "radius": 2 * mm});
            skCircle(sketch, "E15.10.7.0", {"center": v(22.72, 67.53) * mm, "radius": 2 * mm});
            skCircle(sketch, "E15.10.8.0", {"center": v(15.96, 74.9) * mm, "radius": 2 * mm});
            skCircle(sketch, "E15.10.9.0", {"center": v(9.2, 82.27) * mm, "radius": 2 * mm});
            skCircle(sketch, "E15.10.10.0", {"center": v(2.44, 89.64) * mm, "radius": 2 * mm});
            skCircle(sketch, "E15.10.11.0", {"center": v(-4.32, 97) * mm, "radius": 2 * mm});
            skCircle(sketch, "E15.10.12.0", {"center": v(-11.08, 104.38) * mm, "radius": 2 * mm});
            skCircle(sketch, "E15.10.13.0", {"center": v(-17.84, 111.75) * mm, "radius": 2 * mm});
            skCircle(sketch, "E15.10.14.0", {"center": v(-24.6, 119.11) * mm, "radius": 2 * mm});
            skCircle(sketch, "E15.10.15.0", {"center": v(-31.36, 126.48) * mm, "radius": 2 * mm});
            skCircle(sketch, "E15.10.16.0", {"center": v(-38.12, 133.85) * mm, "radius": 2 * mm});
            skCircle(sketch, "E15.10.17.0", {"center": v(-44.88, 141.22) * mm, "radius": 2 * mm});
            skCircle(sketch, "E15.10.18.0", {"center": v(-51.64, 148.6) * mm, "radius": 2 * mm});
            skCircle(sketch, "E15.10.19.0", {"center": v(-58.4, 155.96) * mm, "radius": 2 * mm});
            skCircle(sketch, "E15.10.20.0", {"center": v(-65.16, 163.33) * mm, "radius": 2 * mm});
            skCircle(sketch, "E15.10.21.0", {"center": v(-71.92, 170.7) * mm, "radius": 2 * mm});
            skCircle(sketch, "E15.10.22.0", {"center": v(-78.67, 178.07) * mm, "radius": 2 * mm});
            skCircle(sketch, "E15.10.23.0", {"center": v(-85.43, 185.44) * mm, "radius": 2 * mm});
            skCircle(sketch, "E15.10.24.0", {"center": v(-92.2, 192.81) * mm, "radius": 2 * mm});
            skCircle(sketch, "E15.11.0.0", {"center": v(77.03, 23.08) * mm, "radius": 2 * mm});
            skCircle(sketch, "E15.11.1.0", {"center": v(70.27, 30.45) * mm, "radius": 2 * mm});
            skCircle(sketch, "E15.11.2.0", {"center": v(63.51, 37.82) * mm, "radius": 2 * mm});
            skCircle(sketch, "E15.11.3.0", {"center": v(56.76, 45.19) * mm, "radius": 2 * mm});
            skCircle(sketch, "E15.11.4.0", {"center": v(50, 52.56) * mm, "radius": 2 * mm});
            skCircle(sketch, "E15.11.5.0", {"center": v(43.24, 59.93) * mm, "radius": 2 * mm});
            skCircle(sketch, "E15.11.6.0", {"center": v(36.48, 67.3) * mm, "radius": 2 * mm});
            skCircle(sketch, "E15.11.7.0", {"center": v(29.72, 74.67) * mm, "radius": 2 * mm});
            skCircle(sketch, "E15.11.8.0", {"center": v(22.96, 82.04) * mm, "radius": 2 * mm});
            skCircle(sketch, "E15.11.9.0", {"center": v(16.2, 89.4) * mm, "radius": 2 * mm});
            skCircle(sketch, "E15.11.10.0", {"center": v(9.44, 96.77) * mm, "radius": 2 * mm});
            skCircle(sketch, "E15.11.11.0", {"center": v(2.68, 104.14) * mm, "radius": 2 * mm});
            skCircle(sketch, "E15.11.12.0", {"center": v(-4.08, 111.51) * mm, "radius": 2 * mm});
            skCircle(sketch, "E15.11.13.0", {"center": v(-10.84, 118.88) * mm, "radius": 2 * mm});
            skCircle(sketch, "E15.11.14.0", {"center": v(-17.6, 126.25) * mm, "radius": 2 * mm});
            skCircle(sketch, "E15.11.15.0", {"center": v(-24.36, 133.62) * mm, "radius": 2 * mm});
            skCircle(sketch, "E15.11.16.0", {"center": v(-31.12, 141) * mm, "radius": 2 * mm});
            skCircle(sketch, "E15.11.17.0", {"center": v(-37.87, 148.36) * mm, "radius": 2 * mm});
            skCircle(sketch, "E15.11.18.0", {"center": v(-44.63, 155.73) * mm, "radius": 2 * mm});
            skCircle(sketch, "E15.11.19.0", {"center": v(-51.4, 163.1) * mm, "radius": 2 * mm});
            skCircle(sketch, "E15.11.20.0", {"center": v(-58.15, 170.47) * mm, "radius": 2 * mm});
            skCircle(sketch, "E15.11.21.0", {"center": v(-64.91, 177.84) * mm, "radius": 2 * mm});
            skCircle(sketch, "E15.11.22.0", {"center": v(-71.67, 185.21) * mm, "radius": 2 * mm});
            skCircle(sketch, "E15.11.23.0", {"center": v(-78.43, 192.58) * mm, "radius": 2 * mm});
            skCircle(sketch, "E15.11.24.0", {"center": v(-85.2, 199.95) * mm, "radius": 2 * mm});
            skCircle(sketch, "E15.12.0.0", {"center": v(84.04, 30.22) * mm, "radius": 2 * mm});
            skCircle(sketch, "E15.12.1.0", {"center": v(77.28, 37.59) * mm, "radius": 2 * mm});
            skCircle(sketch, "E15.12.2.0", {"center": v(70.52, 44.96) * mm, "radius": 2 * mm});
            skCircle(sketch, "E15.12.3.0", {"center": v(63.76, 52.33) * mm, "radius": 2 * mm});
            skCircle(sketch, "E15.12.4.0", {"center": v(57, 59.7) * mm, "radius": 2 * mm});
            skCircle(sketch, "E15.12.5.0", {"center": v(50.24, 67.06) * mm, "radius": 2 * mm});
            skCircle(sketch, "E15.12.6.0", {"center": v(43.48, 74.43) * mm, "radius": 2 * mm});
            skCircle(sketch, "E15.12.7.0", {"center": v(36.72, 81.8) * mm, "radius": 2 * mm});
            skCircle(sketch, "E15.12.8.0", {"center": v(29.96, 89.17) * mm, "radius": 2 * mm});
            skCircle(sketch, "E15.12.9.0", {"center": v(23.2, 96.54) * mm, "radius": 2 * mm});
            skCircle(sketch, "E15.12.10.0", {"center": v(16.44, 103.91) * mm, "radius": 2 * mm});
            skCircle(sketch, "E15.12.11.0", {"center": v(9.68, 111.28) * mm, "radius": 2 * mm});
            skCircle(sketch, "E15.12.12.0", {"center": v(2.92, 118.65) * mm, "radius": 2 * mm});
            skCircle(sketch, "E15.12.13.0", {"center": v(-3.83, 126.02) * mm, "radius": 2 * mm});
            skCircle(sketch, "E15.12.14.0", {"center": v(-10.6, 133.4) * mm, "radius": 2 * mm});
            skCircle(sketch, "E15.12.15.0", {"center": v(-17.35, 140.76) * mm, "radius": 2 * mm});
            skCircle(sketch, "E15.12.16.0", {"center": v(-24.11, 148.13) * mm, "radius": 2 * mm});
            skCircle(sketch, "E15.12.17.0", {"center": v(-30.87, 155.5) * mm, "radius": 2 * mm});
            skCircle(sketch, "E15.12.18.0", {"center": v(-37.63, 162.87) * mm, "radius": 2 * mm});
            skCircle(sketch, "E15.12.19.0", {"center": v(-44.4, 170.24) * mm, "radius": 2 * mm});
            skCircle(sketch, "E15.12.20.0", {"center": v(-51.15, 177.6) * mm, "radius": 2 * mm});
            skCircle(sketch, "E15.12.21.0", {"center": v(-57.9, 184.98) * mm, "radius": 2 * mm});
            skCircle(sketch, "E15.12.22.0", {"center": v(-64.67, 192.35) * mm, "radius": 2 * mm});
            skCircle(sketch, "E15.12.23.0", {"center": v(-71.43, 199.72) * mm, "radius": 2 * mm});
            skCircle(sketch, "E15.12.24.0", {"center": v(-78.19, 207.09) * mm, "radius": 2 * mm});
            skCircle(sketch, "E15.13.0.0", {"center": v(91.04, 37.36) * mm, "radius": 2 * mm});
            skCircle(sketch, "E15.13.1.0", {"center": v(84.28, 44.72) * mm, "radius": 2 * mm});
            skCircle(sketch, "E15.13.2.0", {"center": v(77.52, 52.1) * mm, "radius": 2 * mm});
            skCircle(sketch, "E15.13.3.0", {"center": v(70.76, 59.46) * mm, "radius": 2 * mm});
            skCircle(sketch, "E15.13.4.0", {"center": v(64, 66.83) * mm, "radius": 2 * mm});
            skCircle(sketch, "E15.13.5.0", {"center": v(57.24, 74.2) * mm, "radius": 2 * mm});
            skCircle(sketch, "E15.13.6.0", {"center": v(50.48, 81.57) * mm, "radius": 2 * mm});
            skCircle(sketch, "E15.13.7.0", {"center": v(43.72, 88.94) * mm, "radius": 2 * mm});
            skCircle(sketch, "E15.13.8.0", {"center": v(36.96, 96.31) * mm, "radius": 2 * mm});
            skCircle(sketch, "E15.13.9.0", {"center": v(30.2, 103.68) * mm, "radius": 2 * mm});
            skCircle(sketch, "E15.13.10.0", {"center": v(23.45, 111.05) * mm, "radius": 2 * mm});
            skCircle(sketch, "E15.13.11.0", {"center": v(16.69, 118.42) * mm, "radius": 2 * mm});
            skCircle(sketch, "E15.13.12.0", {"center": v(9.93, 125.8) * mm, "radius": 2 * mm});
            skCircle(sketch, "E15.13.13.0", {"center": v(3.17, 133.16) * mm, "radius": 2 * mm});
            skCircle(sketch, "E15.13.14.0", {"center": v(-3.6, 140.53) * mm, "radius": 2 * mm});
            skCircle(sketch, "E15.13.15.0", {"center": v(-10.35, 147.9) * mm, "radius": 2 * mm});
            skCircle(sketch, "E15.13.16.0", {"center": v(-17.1, 155.27) * mm, "radius": 2 * mm});
            skCircle(sketch, "E15.13.17.0", {"center": v(-23.87, 162.64) * mm, "radius": 2 * mm});
            skCircle(sketch, "E15.13.18.0", {"center": v(-30.63, 170) * mm, "radius": 2 * mm});
            skCircle(sketch, "E15.13.19.0", {"center": v(-37.39, 177.38) * mm, "radius": 2 * mm});
            skCircle(sketch, "E15.13.20.0", {"center": v(-44.15, 184.75) * mm, "radius": 2 * mm});
            skCircle(sketch, "E15.13.21.0", {"center": v(-50.9, 192.12) * mm, "radius": 2 * mm});
            skCircle(sketch, "E15.13.22.0", {"center": v(-57.67, 199.49) * mm, "radius": 2 * mm});
            skCircle(sketch, "E15.13.23.0", {"center": v(-64.42, 206.86) * mm, "radius": 2 * mm});
            skCircle(sketch, "E15.13.24.0", {"center": v(-71.18, 214.23) * mm, "radius": 2 * mm});
            skCircle(sketch, "E15.14.0.0", {"center": v(98.04, 44.5) * mm, "radius": 2 * mm});
            skCircle(sketch, "E15.14.1.0", {"center": v(91.28, 51.86) * mm, "radius": 2 * mm});
            skCircle(sketch, "E15.14.2.0", {"center": v(84.52, 59.23) * mm, "radius": 2 * mm});
            skCircle(sketch, "E15.14.3.0", {"center": v(77.76, 66.6) * mm, "radius": 2 * mm});
            skCircle(sketch, "E15.14.4.0", {"center": v(71, 73.97) * mm, "radius": 2 * mm});
            skCircle(sketch, "E15.14.5.0", {"center": v(64.25, 81.34) * mm, "radius": 2 * mm});
            skCircle(sketch, "E15.14.6.0", {"center": v(57.49, 88.71) * mm, "radius": 2 * mm});
            skCircle(sketch, "E15.14.7.0", {"center": v(50.73, 96.08) * mm, "radius": 2 * mm});
            skCircle(sketch, "E15.14.8.0", {"center": v(43.97, 103.45) * mm, "radius": 2 * mm});
            skCircle(sketch, "E15.14.9.0", {"center": v(37.2, 110.82) * mm, "radius": 2 * mm});
            skCircle(sketch, "E15.14.10.0", {"center": v(30.45, 118.2) * mm, "radius": 2 * mm});
            skCircle(sketch, "E15.14.11.0", {"center": v(23.7, 125.56) * mm, "radius": 2 * mm});
            skCircle(sketch, "E15.14.12.0", {"center": v(16.93, 132.93) * mm, "radius": 2 * mm});
            skCircle(sketch, "E15.14.13.0", {"center": v(10.17, 140.3) * mm, "radius": 2 * mm});
            skCircle(sketch, "E15.14.14.0", {"center": v(3.41, 147.67) * mm, "radius": 2 * mm});
            skCircle(sketch, "E15.14.15.0", {"center": v(-3.35, 155.04) * mm, "radius": 2 * mm});
            skCircle(sketch, "E15.14.16.0", {"center": v(-10.1, 162.4) * mm, "radius": 2 * mm});
            skCircle(sketch, "E15.14.17.0", {"center": v(-16.87, 169.78) * mm, "radius": 2 * mm});
            skCircle(sketch, "E15.14.18.0", {"center": v(-23.63, 177.15) * mm, "radius": 2 * mm});
            skCircle(sketch, "E15.14.19.0", {"center": v(-30.38, 184.52) * mm, "radius": 2 * mm});
            skCircle(sketch, "E15.14.20.0", {"center": v(-37.14, 191.89) * mm, "radius": 2 * mm});
            skCircle(sketch, "E15.14.21.0", {"center": v(-43.9, 199.26) * mm, "radius": 2 * mm});
            skCircle(sketch, "E15.14.22.0", {"center": v(-50.66, 206.63) * mm, "radius": 2 * mm});
            skCircle(sketch, "E15.14.23.0", {"center": v(-57.42, 214) * mm, "radius": 2 * mm});
            skCircle(sketch, "E15.14.24.0", {"center": v(-64.18, 221.37) * mm, "radius": 2 * mm});
            skCircle(sketch, "E15.15.0.0", {"center": v(105.05, 51.63) * mm, "radius": 2 * mm});
            skCircle(sketch, "E15.15.1.0", {"center": v(98.29, 59) * mm, "radius": 2 * mm});
            skCircle(sketch, "E15.15.2.0", {"center": v(91.53, 66.37) * mm, "radius": 2 * mm});
            skCircle(sketch, "E15.15.3.0", {"center": v(84.77, 73.74) * mm, "radius": 2 * mm});
            skCircle(sketch, "E15.15.4.0", {"center": v(78, 81.11) * mm, "radius": 2 * mm});
            skCircle(sketch, "E15.15.5.0", {"center": v(71.25, 88.48) * mm, "radius": 2 * mm});
            skCircle(sketch, "E15.15.6.0", {"center": v(64.49, 95.85) * mm, "radius": 2 * mm});
            skCircle(sketch, "E15.15.7.0", {"center": v(57.73, 103.22) * mm, "radius": 2 * mm});
            skCircle(sketch, "E15.15.8.0", {"center": v(50.97, 110.59) * mm, "radius": 2 * mm});
            skCircle(sketch, "E15.15.9.0", {"center": v(44.21, 117.96) * mm, "radius": 2 * mm});
            skCircle(sketch, "E15.15.10.0", {"center": v(37.45, 125.33) * mm, "radius": 2 * mm});
            skCircle(sketch, "E15.15.11.0", {"center": v(30.7, 132.7) * mm, "radius": 2 * mm});
            skCircle(sketch, "E15.15.12.0", {"center": v(23.93, 140.07) * mm, "radius": 2 * mm});
            skCircle(sketch, "E15.15.13.0", {"center": v(17.17, 147.44) * mm, "radius": 2 * mm});
            skCircle(sketch, "E15.15.14.0", {"center": v(10.42, 154.8) * mm, "radius": 2 * mm});
            skCircle(sketch, "E15.15.15.0", {"center": v(3.66, 162.18) * mm, "radius": 2 * mm});
            skCircle(sketch, "E15.15.16.0", {"center": v(-3.1, 169.55) * mm, "radius": 2 * mm});
            skCircle(sketch, "E15.15.17.0", {"center": v(-9.86, 176.92) * mm, "radius": 2 * mm});
            skCircle(sketch, "E15.15.18.0", {"center": v(-16.62, 184.29) * mm, "radius": 2 * mm});
            skCircle(sketch, "E15.15.19.0", {"center": v(-23.38, 191.66) * mm, "radius": 2 * mm});
            skCircle(sketch, "E15.15.20.0", {"center": v(-30.14, 199.03) * mm, "radius": 2 * mm});
            skCircle(sketch, "E15.15.21.0", {"center": v(-36.9, 206.4) * mm, "radius": 2 * mm});
            skCircle(sketch, "E15.15.22.0", {"center": v(-43.66, 213.76) * mm, "radius": 2 * mm});
            skCircle(sketch, "E15.15.23.0", {"center": v(-50.42, 221.13) * mm, "radius": 2 * mm});
            skCircle(sketch, "E15.15.24.0", {"center": v(-57.18, 228.5) * mm, "radius": 2 * mm});
            skCircle(sketch, "E15.16.0.0", {"center": v(112.05, 58.77) * mm, "radius": 2 * mm});
            skCircle(sketch, "E15.16.1.0", {"center": v(105.29, 66.14) * mm, "radius": 2 * mm});
            skCircle(sketch, "E15.16.2.0", {"center": v(98.53, 73.5) * mm, "radius": 2 * mm});
            skCircle(sketch, "E15.16.3.0", {"center": v(91.77, 80.88) * mm, "radius": 2 * mm});
            skCircle(sketch, "E15.16.4.0", {"center": v(85.01, 88.25) * mm, "radius": 2 * mm});
            skCircle(sketch, "E15.16.5.0", {"center": v(78.25, 95.62) * mm, "radius": 2 * mm});
            skCircle(sketch, "E15.16.6.0", {"center": v(71.5, 102.99) * mm, "radius": 2 * mm});
            skCircle(sketch, "E15.16.7.0", {"center": v(64.73, 110.36) * mm, "radius": 2 * mm});
            skCircle(sketch, "E15.16.8.0", {"center": v(57.97, 117.73) * mm, "radius": 2 * mm});
            skCircle(sketch, "E15.16.9.0", {"center": v(51.21, 125.1) * mm, "radius": 2 * mm});
            skCircle(sketch, "E15.16.10.0", {"center": v(44.46, 132.47) * mm, "radius": 2 * mm});
            skCircle(sketch, "E15.16.11.0", {"center": v(37.7, 139.84) * mm, "radius": 2 * mm});
            skCircle(sketch, "E15.16.12.0", {"center": v(30.94, 147.2) * mm, "radius": 2 * mm});
            skCircle(sketch, "E15.16.13.0", {"center": v(24.18, 154.58) * mm, "radius": 2 * mm});
            skCircle(sketch, "E15.16.14.0", {"center": v(17.42, 161.95) * mm, "radius": 2 * mm});
            skCircle(sketch, "E15.16.15.0", {"center": v(10.66, 169.32) * mm, "radius": 2 * mm});
            skCircle(sketch, "E15.16.16.0", {"center": v(3.9, 176.68) * mm, "radius": 2 * mm});
            skCircle(sketch, "E15.16.17.0", {"center": v(-2.86, 184.05) * mm, "radius": 2 * mm});
            skCircle(sketch, "E15.16.18.0", {"center": v(-9.62, 191.42) * mm, "radius": 2 * mm});
            skCircle(sketch, "E15.16.19.0", {"center": v(-16.38, 198.8) * mm, "radius": 2 * mm});
            skCircle(sketch, "E15.16.20.0", {"center": v(-23.14, 206.16) * mm, "radius": 2 * mm});
            skCircle(sketch, "E15.16.21.0", {"center": v(-29.9, 213.53) * mm, "radius": 2 * mm});
            skCircle(sketch, "E15.16.22.0", {"center": v(-36.66, 220.9) * mm, "radius": 2 * mm});
            skCircle(sketch, "E15.16.23.0", {"center": v(-43.42, 228.27) * mm, "radius": 2 * mm});
            skCircle(sketch, "E15.16.24.0", {"center": v(-50.17, 235.64) * mm, "radius": 2 * mm});
            skCircle(sketch, "E15.17.0.0", {"center": v(119.05, 65.9) * mm, "radius": 2 * mm});
            skCircle(sketch, "E15.17.1.0", {"center": v(112.3, 73.28) * mm, "radius": 2 * mm});
            skCircle(sketch, "E15.17.2.0", {"center": v(105.53, 80.65) * mm, "radius": 2 * mm});
            skCircle(sketch, "E15.17.3.0", {"center": v(98.77, 88.02) * mm, "radius": 2 * mm});
            skCircle(sketch, "E15.17.4.0", {"center": v(92.01, 95.39) * mm, "radius": 2 * mm});
            skCircle(sketch, "E15.17.5.0", {"center": v(85.26, 102.76) * mm, "radius": 2 * mm});
            skCircle(sketch, "E15.17.6.0", {"center": v(78.5, 110.13) * mm, "radius": 2 * mm});
            skCircle(sketch, "E15.17.7.0", {"center": v(71.74, 117.5) * mm, "radius": 2 * mm});
            skCircle(sketch, "E15.17.8.0", {"center": v(64.98, 124.87) * mm, "radius": 2 * mm});
            skCircle(sketch, "E15.17.9.0", {"center": v(58.22, 132.24) * mm, "radius": 2 * mm});
            skCircle(sketch, "E15.17.10.0", {"center": v(51.46, 139.6) * mm, "radius": 2 * mm});
            skCircle(sketch, "E15.17.11.0", {"center": v(44.7, 146.98) * mm, "radius": 2 * mm});
            skCircle(sketch, "E15.17.12.0", {"center": v(37.94, 154.34) * mm, "radius": 2 * mm});
            skCircle(sketch, "E15.17.13.0", {"center": v(31.18, 161.71) * mm, "radius": 2 * mm});
            skCircle(sketch, "E15.17.14.0", {"center": v(24.42, 169.08) * mm, "radius": 2 * mm});
            skCircle(sketch, "E15.17.15.0", {"center": v(17.66, 176.45) * mm, "radius": 2 * mm});
            skCircle(sketch, "E15.17.16.0", {"center": v(10.9, 183.82) * mm, "radius": 2 * mm});
            skCircle(sketch, "E15.17.17.0", {"center": v(4.14, 191.2) * mm, "radius": 2 * mm});
            skCircle(sketch, "E15.17.18.0", {"center": v(-2.62, 198.56) * mm, "radius": 2 * mm});
            skCircle(sketch, "E15.17.19.0", {"center": v(-9.38, 205.93) * mm, "radius": 2 * mm});
            skCircle(sketch, "E15.17.20.0", {"center": v(-16.13, 213.3) * mm, "radius": 2 * mm});
            skCircle(sketch, "E15.17.21.0", {"center": v(-22.9, 220.67) * mm, "radius": 2 * mm});
            skCircle(sketch, "E15.17.22.0", {"center": v(-29.65, 228.04) * mm, "radius": 2 * mm});
            skCircle(sketch, "E15.17.23.0", {"center": v(-36.41, 235.41) * mm, "radius": 2 * mm});
            skCircle(sketch, "E15.17.24.0", {"center": v(-43.17, 242.78) * mm, "radius": 2 * mm});
            skCircle(sketch, "E15.18.0.0", {"center": v(126.05, 73.05) * mm, "radius": 2 * mm});
            skCircle(sketch, "E15.18.1.0", {"center": v(119.3, 80.42) * mm, "radius": 2 * mm});
            skCircle(sketch, "E15.18.2.0", {"center": v(112.54, 87.79) * mm, "radius": 2 * mm});
            skCircle(sketch, "E15.18.3.0", {"center": v(105.78, 95.16) * mm, "radius": 2 * mm});
            skCircle(sketch, "E15.18.4.0", {"center": v(99.02, 102.53) * mm, "radius": 2 * mm});
            skCircle(sketch, "E15.18.5.0", {"center": v(92.26, 109.9) * mm, "radius": 2 * mm});
            skCircle(sketch, "E15.18.6.0", {"center": v(85.5, 117.27) * mm, "radius": 2 * mm});
            skCircle(sketch, "E15.18.7.0", {"center": v(78.74, 124.63) * mm, "radius": 2 * mm});
            skCircle(sketch, "E15.18.8.0", {"center": v(71.98, 132) * mm, "radius": 2 * mm});
            skCircle(sketch, "E15.18.9.0", {"center": v(65.22, 139.37) * mm, "radius": 2 * mm});
            skCircle(sketch, "E15.18.10.0", {"center": v(58.46, 146.74) * mm, "radius": 2 * mm});
            skCircle(sketch, "E15.18.11.0", {"center": v(51.7, 154.11) * mm, "radius": 2 * mm});
            skCircle(sketch, "E15.18.12.0", {"center": v(44.94, 161.48) * mm, "radius": 2 * mm});
            skCircle(sketch, "E15.18.13.0", {"center": v(38.18, 168.85) * mm, "radius": 2 * mm});
            skCircle(sketch, "E15.18.14.0", {"center": v(31.42, 176.22) * mm, "radius": 2 * mm});
            skCircle(sketch, "E15.18.15.0", {"center": v(24.67, 183.6) * mm, "radius": 2 * mm});
            skCircle(sketch, "E15.18.16.0", {"center": v(17.9, 190.96) * mm, "radius": 2 * mm});
            skCircle(sketch, "E15.18.17.0", {"center": v(11.15, 198.33) * mm, "radius": 2 * mm});
            skCircle(sketch, "E15.18.18.0", {"center": v(4.39, 205.7) * mm, "radius": 2 * mm});
            skCircle(sketch, "E15.18.19.0", {"center": v(-2.37, 213.07) * mm, "radius": 2 * mm});
            skCircle(sketch, "E15.18.20.0", {"center": v(-9.13, 220.44) * mm, "radius": 2 * mm});
            skCircle(sketch, "E15.18.21.0", {"center": v(-15.9, 227.81) * mm, "radius": 2 * mm});
            skCircle(sketch, "E15.18.22.0", {"center": v(-22.65, 235.18) * mm, "radius": 2 * mm});
            skCircle(sketch, "E15.18.23.0", {"center": v(-29.4, 242.55) * mm, "radius": 2 * mm});
            skCircle(sketch, "E15.18.24.0", {"center": v(-36.17, 249.92) * mm, "radius": 2 * mm});
            skCircle(sketch, "E15.19.0.0", {"center": v(133.06, 80.19) * mm, "radius": 2 * mm});
            skCircle(sketch, "E15.19.1.0", {"center": v(126.3, 87.56) * mm, "radius": 2 * mm});
            skCircle(sketch, "E15.19.2.0", {"center": v(119.54, 94.93) * mm, "radius": 2 * mm});
            skCircle(sketch, "E15.19.3.0", {"center": v(112.78, 102.3) * mm, "radius": 2 * mm});
            skCircle(sketch, "E15.19.4.0", {"center": v(106.02, 109.66) * mm, "radius": 2 * mm});
            skCircle(sketch, "E15.19.5.0", {"center": v(99.26, 117.03) * mm, "radius": 2 * mm});
            skCircle(sketch, "E15.19.6.0", {"center": v(92.5, 124.4) * mm, "radius": 2 * mm});
            skCircle(sketch, "E15.19.7.0", {"center": v(85.74, 131.77) * mm, "radius": 2 * mm});
            skCircle(sketch, "E15.19.8.0", {"center": v(78.98, 139.14) * mm, "radius": 2 * mm});
            skCircle(sketch, "E15.19.9.0", {"center": v(72.22, 146.51) * mm, "radius": 2 * mm});
            skCircle(sketch, "E15.19.10.0", {"center": v(65.46, 153.88) * mm, "radius": 2 * mm});
            skCircle(sketch, "E15.19.11.0", {"center": v(58.7, 161.25) * mm, "radius": 2 * mm});
            skCircle(sketch, "E15.19.12.0", {"center": v(51.95, 168.62) * mm, "radius": 2 * mm});
            skCircle(sketch, "E15.19.13.0", {"center": v(45.19, 176) * mm, "radius": 2 * mm});
            skCircle(sketch, "E15.19.14.0", {"center": v(38.43, 183.36) * mm, "radius": 2 * mm});
            skCircle(sketch, "E15.19.15.0", {"center": v(31.67, 190.73) * mm, "radius": 2 * mm});
            skCircle(sketch, "E15.19.16.0", {"center": v(24.9, 198.1) * mm, "radius": 2 * mm});
            skCircle(sketch, "E15.19.17.0", {"center": v(18.15, 205.47) * mm, "radius": 2 * mm});
            skCircle(sketch, "E15.19.18.0", {"center": v(11.4, 212.84) * mm, "radius": 2 * mm});
            skCircle(sketch, "E15.19.19.0", {"center": v(4.63, 220.2) * mm, "radius": 2 * mm});
            skCircle(sketch, "E15.19.20.0", {"center": v(-2.13, 227.58) * mm, "radius": 2 * mm});
            skCircle(sketch, "E15.19.21.0", {"center": v(-8.89, 234.95) * mm, "radius": 2 * mm});
            skCircle(sketch, "E15.19.22.0", {"center": v(-15.65, 242.32) * mm, "radius": 2 * mm});
            skCircle(sketch, "E15.19.23.0", {"center": v(-22.4, 249.69) * mm, "radius": 2 * mm});
            skCircle(sketch, "E15.19.24.0", {"center": v(-29.17, 257.06) * mm, "radius": 2 * mm});
            skCircle(sketch, "E15.20.0.0", {"center": v(140.06, 87.32) * mm, "radius": 2 * mm});
            skCircle(sketch, "E15.20.1.0", {"center": v(133.3, 94.7) * mm, "radius": 2 * mm});
            skCircle(sketch, "E15.20.2.0", {"center": v(126.54, 102.06) * mm, "radius": 2 * mm});
            skCircle(sketch, "E15.20.3.0", {"center": v(119.78, 109.43) * mm, "radius": 2 * mm});
            skCircle(sketch, "E15.20.4.0", {"center": v(113.02, 116.8) * mm, "radius": 2 * mm});
            skCircle(sketch, "E15.20.5.0", {"center": v(106.26, 124.17) * mm, "radius": 2 * mm});
            skCircle(sketch, "E15.20.6.0", {"center": v(99.5, 131.54) * mm, "radius": 2 * mm});
            skCircle(sketch, "E15.20.7.0", {"center": v(92.75, 138.91) * mm, "radius": 2 * mm});
            skCircle(sketch, "E15.20.8.0", {"center": v(85.99, 146.28) * mm, "radius": 2 * mm});
            skCircle(sketch, "E15.20.9.0", {"center": v(79.23, 153.65) * mm, "radius": 2 * mm});
            skCircle(sketch, "E15.20.10.0", {"center": v(72.47, 161.02) * mm, "radius": 2 * mm});
            skCircle(sketch, "E15.20.11.0", {"center": v(65.7, 168.4) * mm, "radius": 2 * mm});
            skCircle(sketch, "E15.20.12.0", {"center": v(58.95, 175.76) * mm, "radius": 2 * mm});
            skCircle(sketch, "E15.20.13.0", {"center": v(52.19, 183.13) * mm, "radius": 2 * mm});
            skCircle(sketch, "E15.20.14.0", {"center": v(45.43, 190.5) * mm, "radius": 2 * mm});
            skCircle(sketch, "E15.20.15.0", {"center": v(38.67, 197.87) * mm, "radius": 2 * mm});
            skCircle(sketch, "E15.20.16.0", {"center": v(31.91, 205.24) * mm, "radius": 2 * mm});
            skCircle(sketch, "E15.20.17.0", {"center": v(25.15, 212.6) * mm, "radius": 2 * mm});
            skCircle(sketch, "E15.20.18.0", {"center": v(18.4, 219.98) * mm, "radius": 2 * mm});
            skCircle(sketch, "E15.20.19.0", {"center": v(11.63, 227.35) * mm, "radius": 2 * mm});
            skCircle(sketch, "E15.20.20.0", {"center": v(4.87, 234.72) * mm, "radius": 2 * mm});
            skCircle(sketch, "E15.20.21.0", {"center": v(-1.88, 242.09) * mm, "radius": 2 * mm});
            skCircle(sketch, "E15.20.22.0", {"center": v(-8.64, 249.46) * mm, "radius": 2 * mm});
            skCircle(sketch, "E15.20.23.0", {"center": v(-15.4, 256.83) * mm, "radius": 2 * mm});
            skCircle(sketch, "E15.20.24.0", {"center": v(-22.16, 264.2) * mm, "radius": 2 * mm});
            skCircle(sketch, "E15.21.0.0", {"center": v(147.06, 94.46) * mm, "radius": 2 * mm});
            skCircle(sketch, "E15.21.1.0", {"center": v(140.3, 101.83) * mm, "radius": 2 * mm});
            skCircle(sketch, "E15.21.2.0", {"center": v(133.55, 109.2) * mm, "radius": 2 * mm});
            skCircle(sketch, "E15.21.3.0", {"center": v(126.79, 116.57) * mm, "radius": 2 * mm});
            skCircle(sketch, "E15.21.4.0", {"center": v(120.03, 123.94) * mm, "radius": 2 * mm});
            skCircle(sketch, "E15.21.5.0", {"center": v(113.27, 131.31) * mm, "radius": 2 * mm});
            skCircle(sketch, "E15.21.6.0", {"center": v(106.5, 138.68) * mm, "radius": 2 * mm});
            skCircle(sketch, "E15.21.7.0", {"center": v(99.75, 146.05) * mm, "radius": 2 * mm});
            skCircle(sketch, "E15.21.8.0", {"center": v(92.99, 153.42) * mm, "radius": 2 * mm});
            skCircle(sketch, "E15.21.9.0", {"center": v(86.23, 160.79) * mm, "radius": 2 * mm});
            skCircle(sketch, "E15.21.10.0", {"center": v(79.47, 168.16) * mm, "radius": 2 * mm});
            skCircle(sketch, "E15.21.11.0", {"center": v(72.71, 175.53) * mm, "radius": 2 * mm});
            skCircle(sketch, "E15.21.12.0", {"center": v(65.95, 182.9) * mm, "radius": 2 * mm});
            skCircle(sketch, "E15.21.13.0", {"center": v(59.2, 190.27) * mm, "radius": 2 * mm});
            skCircle(sketch, "E15.21.14.0", {"center": v(52.43, 197.64) * mm, "radius": 2 * mm});
            skCircle(sketch, "E15.21.15.0", {"center": v(45.67, 205) * mm, "radius": 2 * mm});
            skCircle(sketch, "E15.21.16.0", {"center": v(38.91, 212.38) * mm, "radius": 2 * mm});
            skCircle(sketch, "E15.21.17.0", {"center": v(32.16, 219.75) * mm, "radius": 2 * mm});
            skCircle(sketch, "E15.21.18.0", {"center": v(25.4, 227.12) * mm, "radius": 2 * mm});
            skCircle(sketch, "E15.21.19.0", {"center": v(18.64, 234.49) * mm, "radius": 2 * mm});
            skCircle(sketch, "E15.21.20.0", {"center": v(11.88, 241.86) * mm, "radius": 2 * mm});
            skCircle(sketch, "E15.21.21.0", {"center": v(5.12, 249.23) * mm, "radius": 2 * mm});
            skCircle(sketch, "E15.21.22.0", {"center": v(-1.64, 256.6) * mm, "radius": 2 * mm});
            skCircle(sketch, "E15.21.23.0", {"center": v(-8.4, 263.96) * mm, "radius": 2 * mm});
            skCircle(sketch, "E15.21.24.0", {"center": v(-15.16, 271.33) * mm, "radius": 2 * mm});
            skCircle(sketch, "E15.22.0.0", {"center": v(154.07, 101.6) * mm, "radius": 2 * mm});
            skCircle(sketch, "E15.22.1.0", {"center": v(147.3, 108.97) * mm, "radius": 2 * mm});
            skCircle(sketch, "E15.22.2.0", {"center": v(140.55, 116.34) * mm, "radius": 2 * mm});
            skCircle(sketch, "E15.22.3.0", {"center": v(133.79, 123.71) * mm, "radius": 2 * mm});
            skCircle(sketch, "E15.22.4.0", {"center": v(127.03, 131.08) * mm, "radius": 2 * mm});
            skCircle(sketch, "E15.22.5.0", {"center": v(120.27, 138.45) * mm, "radius": 2 * mm});
            skCircle(sketch, "E15.22.6.0", {"center": v(113.51, 145.82) * mm, "radius": 2 * mm});
            skCircle(sketch, "E15.22.7.0", {"center": v(106.75, 153.19) * mm, "radius": 2 * mm});
            skCircle(sketch, "E15.22.8.0", {"center": v(100, 160.56) * mm, "radius": 2 * mm});
            skCircle(sketch, "E15.22.9.0", {"center": v(93.23, 167.93) * mm, "radius": 2 * mm});
            skCircle(sketch, "E15.22.10.0", {"center": v(86.47, 175.3) * mm, "radius": 2 * mm});
            skCircle(sketch, "E15.22.11.0", {"center": v(79.71, 182.67) * mm, "radius": 2 * mm});
            skCircle(sketch, "E15.22.12.0", {"center": v(72.96, 190.04) * mm, "radius": 2 * mm});
            skCircle(sketch, "E15.22.13.0", {"center": v(66.2, 197.4) * mm, "radius": 2 * mm});
            skCircle(sketch, "E15.22.14.0", {"center": v(59.44, 204.78) * mm, "radius": 2 * mm});
            skCircle(sketch, "E15.22.15.0", {"center": v(52.68, 212.15) * mm, "radius": 2 * mm});
            skCircle(sketch, "E15.22.16.0", {"center": v(45.92, 219.52) * mm, "radius": 2 * mm});
            skCircle(sketch, "E15.22.17.0", {"center": v(39.16, 226.89) * mm, "radius": 2 * mm});
            skCircle(sketch, "E15.22.18.0", {"center": v(32.4, 234.25) * mm, "radius": 2 * mm});
            skCircle(sketch, "E15.22.19.0", {"center": v(25.64, 241.62) * mm, "radius": 2 * mm});
            skCircle(sketch, "E15.22.20.0", {"center": v(18.88, 249) * mm, "radius": 2 * mm});
            skCircle(sketch, "E15.22.21.0", {"center": v(12.12, 256.36) * mm, "radius": 2 * mm});
            skCircle(sketch, "E15.22.22.0", {"center": v(5.36, 263.73) * mm, "radius": 2 * mm});
            skCircle(sketch, "E15.22.23.0", {"center": v(-1.4, 271.1) * mm, "radius": 2 * mm});
            skCircle(sketch, "E15.22.24.0", {"center": v(-8.16, 278.47) * mm, "radius": 2 * mm});
            skCircle(sketch, "E15.23.0.0", {"center": v(161.07, 108.74) * mm, "radius": 2 * mm});
            skCircle(sketch, "E15.23.1.0", {"center": v(154.31, 116.1) * mm, "radius": 2 * mm});
            skCircle(sketch, "E15.23.2.0", {"center": v(147.55, 123.48) * mm, "radius": 2 * mm});
            skCircle(sketch, "E15.23.3.0", {"center": v(140.8, 130.85) * mm, "radius": 2 * mm});
            skCircle(sketch, "E15.23.4.0", {"center": v(134.03, 138.22) * mm, "radius": 2 * mm});
            skCircle(sketch, "E15.23.5.0", {"center": v(127.27, 145.59) * mm, "radius": 2 * mm});
            skCircle(sketch, "E15.23.6.0", {"center": v(120.51, 152.96) * mm, "radius": 2 * mm});
            skCircle(sketch, "E15.23.7.0", {"center": v(113.75, 160.33) * mm, "radius": 2 * mm});
            skCircle(sketch, "E15.23.8.0", {"center": v(107, 167.7) * mm, "radius": 2 * mm});
            skCircle(sketch, "E15.23.9.0", {"center": v(100.24, 175.07) * mm, "radius": 2 * mm});
            skCircle(sketch, "E15.23.10.0", {"center": v(93.48, 182.44) * mm, "radius": 2 * mm});
            skCircle(sketch, "E15.23.11.0", {"center": v(86.72, 189.8) * mm, "radius": 2 * mm});
            skCircle(sketch, "E15.23.12.0", {"center": v(79.96, 197.18) * mm, "radius": 2 * mm});
            skCircle(sketch, "E15.23.13.0", {"center": v(73.2, 204.55) * mm, "radius": 2 * mm});
            skCircle(sketch, "E15.23.14.0", {"center": v(66.44, 211.91) * mm, "radius": 2 * mm});
            skCircle(sketch, "E15.23.15.0", {"center": v(59.68, 219.28) * mm, "radius": 2 * mm});
            skCircle(sketch, "E15.23.16.0", {"center": v(52.92, 226.65) * mm, "radius": 2 * mm});
            skCircle(sketch, "E15.23.17.0", {"center": v(46.16, 234.02) * mm, "radius": 2 * mm});
            skCircle(sketch, "E15.23.18.0", {"center": v(39.4, 241.4) * mm, "radius": 2 * mm});
            skCircle(sketch, "E15.23.19.0", {"center": v(32.64, 248.76) * mm, "radius": 2 * mm});
            skCircle(sketch, "E15.23.20.0", {"center": v(25.88, 256.13) * mm, "radius": 2 * mm});
            skCircle(sketch, "E15.23.21.0", {"center": v(19.12, 263.5) * mm, "radius": 2 * mm});
            skCircle(sketch, "E15.23.22.0", {"center": v(12.37, 270.87) * mm, "radius": 2 * mm});
            skCircle(sketch, "E15.23.23.0", {"center": v(5.6, 278.24) * mm, "radius": 2 * mm});
            skCircle(sketch, "E15.23.24.0", {"center": v(-1.15, 285.61) * mm, "radius": 2 * mm});
            skCircle(sketch, "E15.24.0.0", {"center": v(168.07, 115.88) * mm, "radius": 2 * mm});
            skCircle(sketch, "E15.24.1.0", {"center": v(161.31, 123.25) * mm, "radius": 2 * mm});
            skCircle(sketch, "E15.24.2.0", {"center": v(154.55, 130.62) * mm, "radius": 2 * mm});
            skCircle(sketch, "E15.24.3.0", {"center": v(147.8, 137.99) * mm, "radius": 2 * mm});
            skCircle(sketch, "E15.24.4.0", {"center": v(141.04, 145.36) * mm, "radius": 2 * mm});
            skCircle(sketch, "E15.24.5.0", {"center": v(134.28, 152.73) * mm, "radius": 2 * mm});
            skCircle(sketch, "E15.24.6.0", {"center": v(127.52, 160.1) * mm, "radius": 2 * mm});
            skCircle(sketch, "E15.24.7.0", {"center": v(120.76, 167.47) * mm, "radius": 2 * mm});
            skCircle(sketch, "E15.24.8.0", {"center": v(114, 174.84) * mm, "radius": 2 * mm});
            skCircle(sketch, "E15.24.9.0", {"center": v(107.24, 182.2) * mm, "radius": 2 * mm});
            skCircle(sketch, "E15.24.10.0", {"center": v(100.48, 189.57) * mm, "radius": 2 * mm});
            skCircle(sketch, "E15.24.11.0", {"center": v(93.72, 196.94) * mm, "radius": 2 * mm});
            skCircle(sketch, "E15.24.12.0", {"center": v(86.96, 204.31) * mm, "radius": 2 * mm});
            skCircle(sketch, "E15.24.13.0", {"center": v(80.2, 211.68) * mm, "radius": 2 * mm});
            skCircle(sketch, "E15.24.14.0", {"center": v(73.44, 219.05) * mm, "radius": 2 * mm});
            skCircle(sketch, "E15.24.15.0", {"center": v(66.68, 226.42) * mm, "radius": 2 * mm});
            skCircle(sketch, "E15.24.16.0", {"center": v(59.92, 233.8) * mm, "radius": 2 * mm});
            skCircle(sketch, "E15.24.17.0", {"center": v(53.16, 241.16) * mm, "radius": 2 * mm});
            skCircle(sketch, "E15.24.18.0", {"center": v(46.4, 248.53) * mm, "radius": 2 * mm});
            skCircle(sketch, "E15.24.19.0", {"center": v(39.65, 255.9) * mm, "radius": 2 * mm});
            skCircle(sketch, "E15.24.20.0", {"center": v(32.89, 263.27) * mm, "radius": 2 * mm});
            skCircle(sketch, "E15.24.21.0", {"center": v(26.13, 270.64) * mm, "radius": 2 * mm});
            skCircle(sketch, "E15.24.22.0", {"center": v(19.37, 278.01) * mm, "radius": 2 * mm});
            skCircle(sketch, "E15.24.23.0", {"center": v(12.6, 285.38) * mm, "radius": 2 * mm});
            skCircle(sketch, "E15.24.24.0", {"center": v(5.85, 292.75) * mm, "radius": 2 * mm});
            skLineSegment(sketch, "E15.direction1", {"start": v(0, -55.44) * mm, "end": v(7, -48.3) * mm, "construction": true});
            skLineSegment(sketch, "E15.direction2", {"start": v(0, -55.44) * mm, "end": v(-6.76, -48.08) * mm, "construction": true});
            skSolve(sketch);
        }
        {
            var Q0;
            Q0 = qSketchRegion(id + "F29", true);
            extrude(context, id + "F30", {"entities" : qUnion([Q0]), "operationType" : NewBodyOperationType.REMOVE, "endBound" : BoundingType.SYMMETRIC, "oppositeDirection" : true, "depth" : 155 * mm, "offsetDistance" : 25 * mm});
        }
    });
